# Revit family: Plumbing-Valves-Sloan-SOLIS-RESS-Cz
name_source: partatom
category: Plumbing Fixtures
units: mm (PartAtom-declared; Revit-internal decimal feet)

## family parameters
Cut with Voids When Loaded = No
Host = Face
OmniClass Number = 23.45.05.14.99
OmniClass Title = Other Sanitary Washing Plumbing Fixtures
Part Type = Normal
Room Calculation Point = No
Round Connector Dimension = Use Diameter
Shared = No

## types (9) — shared parameters
Assembly Code = D2020300
CW Connection = Yes
Centerline of Supply from Top of Fixture = 11 1/2"
Centerline of Supply to Centerline of Valve = 4 3/4"
Default Elevation = 0"
Edition number = 1
HW Connection = No
Height = 16 1/2"
Keynote = 15410
Manufacturer = Sloan Valve
Operating Water Pressure = 15 – 80 PSI (103 – 552 kPa)
Product Material = Sloan Valve - Finish - Polished Chrome
Product data url = https://www.bimobject.com
URL = www.sloanvalve.com
Valve Pressure Drop = 0.00 psi
Vent Connection = No
Waste Connection = No
Water Inlet Connection Diameter = 1"
zero-valued in all types: CWFU, HWFU, WFU

## per-type parameters (varying)
| type | Description | Flush Rate | Part Number |
| SOLIS RESS-C-1.6-XDT-OR | 1.6 gpf, Polished Chrome Finish, Fixture Connection Top Spud, Single Flush, Adjustable Ground Joint for Tek Control Stop, Electrical Override, Solar, SOLIS® Exposed Sensor Water Closet Retrofit Flushometer. | 1.6 gpf (6.0 Lpf) | 3370052 |
| SOLIS RESS-C-1.6-DFB-OR-Z | 1.6 gpf, Dual-Filtered Fixed Bypass Diaphragm, Polished Chrome Finish, Fixture Connection Top Spud, Single Flush, Electrical Override, Solar, Fits Zurn† valve bodies, SOLIS® Exposed Sensor Water Closet Retrofit Flushometer. | 1.6 gpf (6.0 Lpf) | 3375325 |
| SOLIS RESS-C-1.28-OR | 1.28 gpf, Polished Chrome Finish, Fixture Connection Top Spud, Single Flush, Electrical Override, Solar, SOLIS® Exposed Sensor Water Closet Retrofit Flushometer. | 1.28 gpf (4.8 Lpf) | 3375302 |
| SOLIS RESS-C-1.6/3.5-OR-Z | 1.6/3.5 gpf, Polished Chrome Finish, Fixture Connection Top Spud, Single Flush, Electrical Override, Solar, Fits Zurn† valve bodies, SOLIS® Exposed Sensor Water Closet Retrofit Flushometer. | 1.6/3.5 gpf (6.0/13.2 Lpf) | 3375320 |
| SOLIS RESS-C-1.6/1.1-OR | 1.6/1.1 gpf, Polished Chrome Finish, Fixture Connection Top Spud, Dual Flush, Electrical Override, Solar, SOLIS® Exposed Sensor Water Closet Retrofit Flushometer | 1.6/1.1 gpf (6.0/4.2 Lpf) | 3375300 |
| SOLIS RESS-C-1.6-OR | 1.6 gpf, Polished Chrome Finish, Fixture Connection Top Spud, Single Flush, Electrical Override, Solar, SOLIS® Exposed Sensor Water Closet Retrofit Flushometer. | 1.6 gpf (6.0 Lpf) | 3375301 |
| SOLIS RESS-C-1.6/1.1-XDT-OR | 1.6/1.1 gpf, Polished Chrome Finish, Fixture Connection Top Spud, Dual Flush, Adjustable Ground Joint for Tek Control Stop, Electrical Override, Solar, SOLIS® Exposed Sensor Water Closet Retrofit Flushometer | 1.6/1.1 gpf (6.0/4.2 Lpf) | 3370050 |
| SOLIS RESS-C-1.28-OR-Z | 1.28 gpf, Polished Chrome Finish, Fixture Connection Top Spud, Single Flush, Electrical Override, Solar, Fits Zurn† valve bodies, SOLIS® Exposed Sensor Water Closet Retrofit Flushometer. | 1.28 gpf (4.8 Lpf) | 3375346 |
| SOLIS RESS-C-1.6/1.1-XD-OR | 1.6/1.1 gpf, Polished Chrome Finish, Fixture Connection Top Spud, Dual Flush, No Control Stop, Electrical Override, Solar, SOLIS® Exposed Sensor Water Closet Retrofit Flushometer | 1.6/1.1 gpf (6.0/4.2 Lpf) | 3375345 |

note: column(s) folded — value = type name in every type: Model

## geometry (parser evidence)
native form markers: Sweep x6
no freeform markers — native parametric forms only
